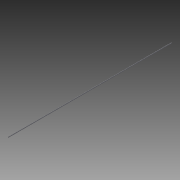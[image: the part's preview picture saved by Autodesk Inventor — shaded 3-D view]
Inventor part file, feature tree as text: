
AUTODESK INVENTOR PART (.ipt)
format: ipt  version: 2013 (Build 170138000, 138)  size: 76,288 bytes
history: native  units: in
note: dims shown in document units (in); Inventor stores cm internally (conversion verified against a paired STEP export)
features: plane x1, extrude x1, sketch x1
ambient origin geometry x8: Origin, YZ Plane, XZ Plane, XY Plane, X Axis, Y Axis, Z Axis, Center Point
feature tree (3):
  plane  "Work Plane1"
  extrude  "Extrusion1"  [1 undecoded]
  sketch  "Sketch1"  dims[d0=72.5in d1=0.0in]
note: 1 required parameter value undecoded (feature->parameter linkage not recoverable at this tier; creation-order binding heuristic only, values carry confidence <= 0.55)
